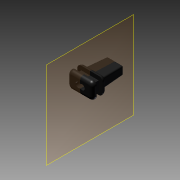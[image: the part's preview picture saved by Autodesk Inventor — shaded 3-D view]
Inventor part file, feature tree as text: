
AUTODESK INVENTOR PART (.ipt)
format: ipt  version: 2013 (Build 170138000, 138)  size: 266,240 bytes
history: native  units: in
note: dims shown in document units (in); Inventor stores cm internally (conversion verified against a paired STEP export)
features: sketch x5, plane x4, extrude x3, fillet x2, mirror x1, loft x1
ambient origin geometry x8: Origin, YZ Plane, XZ Plane, XY Plane, X Axis, Y Axis, Z Axis, Center Point
bodies: Solid1 (feature_tree)
feature tree (16):
  sketch  "Sketch1"  dims[d0=0.039in d1=0.0in d2=0.059in d3=0.0in]
  extrude  "Extrusion1"  Depth=0.059in TaperAngle=0.0deg
  extrude  "Extrusion2"  Depth=0.213in
  fillet  "Fillet1"  Radius=0.16in
  plane  "Work Plane1"
  mirror  "Mirror1"
  sketch  "Sketch2"  dims[d4=0.034in d6=0.213in d7=0.16in]
  plane  "Work Plane3"
  sketch  "Sketch3"  dims[d8=0.081in d9=0.0in d10=90.0deg]
  plane  "Work Plane4"
  loft  "Loft1"
  extrude  "Extrusion3"  Depth=0.213in TaperAngle=0.0deg
  fillet  "Fillet3"  Radius=0.0125in
  plane  "Work Plane5"
  sketch  "Sketch4"  dims[d11=0.0in d12=90.0deg d14=0.213in d15=0.0in d16=0.0125in]
  sketch  "Sketch5"  dims[d17=0.0125in d18=0.0123in]
